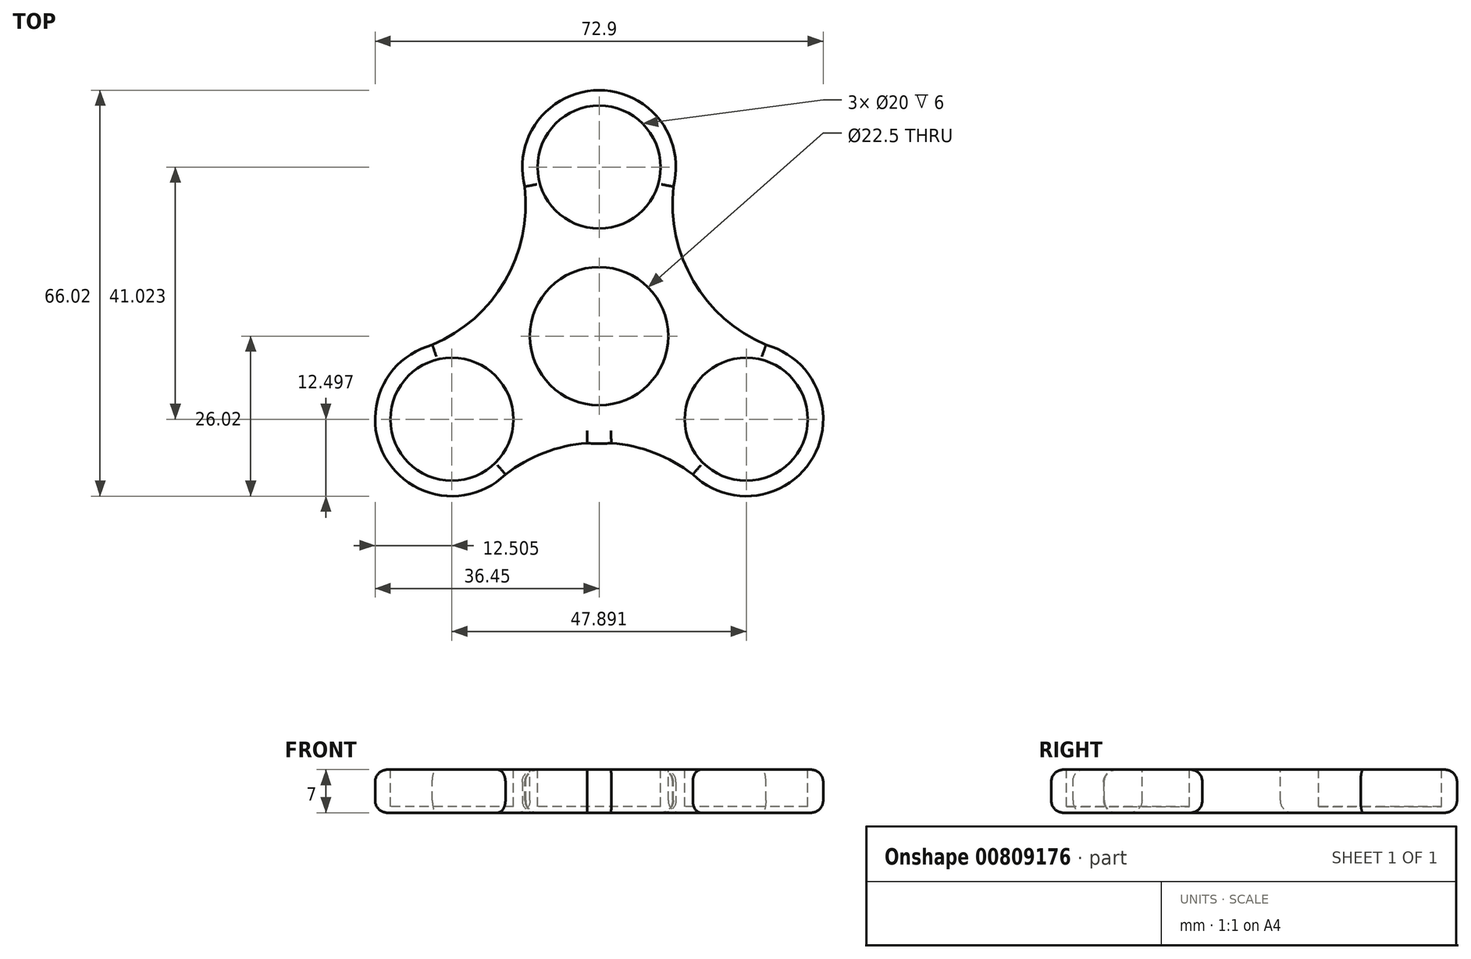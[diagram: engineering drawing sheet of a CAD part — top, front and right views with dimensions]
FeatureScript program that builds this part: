
annotation { "Feature Type Name" : "Feature", "Feature Type Description" : "" }
export const myFeature = defineFeature(function(context is Context, id is Id, definition is map)
    precondition{}
    {
        {
            var Q0;
            Q0=qCreatedBy(makeId("Top.planeOp"),FACE);
            var sketch = newSketch(context, id + "F0", { "sketchPlane" : qUnion([Q0])});
            skCircle(sketch, "E0", {"center": v(0, 0) * mm, "radius": 17.5 * mm});
            skCircle(sketch, "E1", {"center": v(0, 27.5) * mm, "radius": 12.5 * mm});
            skCircle(sketch, "E2", {"center": v(-23.95, -13.52) * mm, "radius": 12.5 * mm});
            skCircle(sketch, "E3", {"center": v(23.95, -13.52) * mm, "radius": 12.5 * mm});
            skSolve(sketch);
        }
        {
            var Q0;
            Q0 = qSketchRegion(id + "F0", true);
            extrude(context, id + "F1", {"entities" : qUnion([Q0]), "depth" : 7 * mm, "offsetDistance" : 25 * mm});
        }
        {
            var Q0;
            Q0=makeQuery(id+"F1.opExtrude","CAP_FACE",FACE,{"disambiguationData":[OSD([sQuery(id+"F0.wireOp",EDGE,"E0"),sQuery(id+"F0.wireOp",EDGE,"E1"),sQuery(id+"F0.wireOp",EDGE,"E2"),sQuery(id+"F0.wireOp",EDGE,"E3")])],"isStart":false});
            var sketch = newSketch(context, id + "F2", { "sketchPlane" : qUnion([Q0])});
            skCircle(sketch, "E4", {"center": v(0, 0) * mm, "radius": 11.25 * mm});
            skSolve(sketch);
        }
        {
            var Q0;
            Q0 = qSketchRegion(id + "F2", true);
            extrude(context, id + "F3", {"entities" : qUnion([Q0]), "operationType" : NewBodyOperationType.REMOVE, "endBound" : BoundingType.THROUGH_ALL, "oppositeDirection" : true, "depth" : 25 * mm, "offsetDistance" : 25 * mm});
        }
        {
            var Q0;
            Q0=makeQuery(id+"F1.opExtrude","CAP_FACE",FACE,{"disambiguationData":[OSD([sQuery(id+"F0.wireOp",EDGE,"E0"),sQuery(id+"F0.wireOp",EDGE,"E1"),sQuery(id+"F0.wireOp",EDGE,"E2"),sQuery(id+"F0.wireOp",EDGE,"E3")])],"isStart":false});
            var sketch = newSketch(context, id + "F4", { "sketchPlane" : qUnion([Q0])});
            skCircle(sketch, "E5", {"center": v(0, 27.5) * mm, "radius": 10 * mm});
            skCircle(sketch, "E6", {"center": v(23.95, -13.52) * mm, "radius": 10 * mm});
            skCircle(sketch, "E7", {"center": v(-23.95, -13.52) * mm, "radius": 10 * mm});
            skSolve(sketch);
        }
        {
            var Q0;
            Q0 = qSketchRegion(id + "F4", true);
            extrude(context, id + "F5", {"entities" : qUnion([Q0]), "operationType" : NewBodyOperationType.REMOVE, "oppositeDirection" : true, "depth" : 6 * mm, "offsetDistance" : 25 * mm});
        }
        {
            var Q0;
            Q0=makeQuery(id+"F1.opExtrude","CAP_FACE",FACE,{"disambiguationData":[OSD([sQuery(id+"F0.wireOp",EDGE,"E0"),sQuery(id+"F0.wireOp",EDGE,"E1"),sQuery(id+"F0.wireOp",EDGE,"E2"),sQuery(id+"F0.wireOp",EDGE,"E3")])],"isStart":false});
            var sketch = newSketch(context, id + "F6", { "sketchPlane" : qUnion([Q0])});
            skArc(sketch, "E8", {"start": v(15.24, -22.5) * mm, "mid": v(0, -17.31) * mm, "end": v(-15.24, -22.5) * mm});
            skArc(sketch, "E9", {"start": v(-27.13, -1.43) * mm, "mid": v(-15.35, 8.96) * mm, "end": v(-12.1, 24.33) * mm});
            skArc(sketch, "E10", {"start": v(12.1, 24.33) * mm, "mid": v(15.35, 8.96) * mm, "end": v(27.13, -1.43) * mm});
            skSolve(sketch);
        }
        {
            var Q0;
            {var subQ0=sQuery(id+"F6.wireOp",EDGE,"E9");Q0=makeQuery(id+"F6.imprint","IMPRINT",FACE,{"disambiguationData":[TD([[makeQuery(id+"F6.imprint","IMPRINT",EDGE,{"derivedFrom":subQ0}),-1.0]])]});}
            var Q1;
            {var subQ0=sQuery(id+"F6.wireOp",EDGE,"E8");var subQ1=sQuery(id+"F0.wireOp",EDGE,"E2");var subQ2=makeQuery(id+"F1.opExtrude","CAP_EDGE",EDGE,{"disambiguationData":[OSD([subQ1])],"isStart":false});var subQ3=makeQuery(id+"F6.imprint","INTERSECT",VERTEX,{"derivedFrom":[subQ2,subQ0]});Q1=makeQuery(id+"F6.imprint","IMPRINT",FACE,{"disambiguationData":[TD([[makeQuery(id+"F6.imprint","IMPRINT",EDGE,{"disambiguationData":[TD([[subQ3,1.0]])],"derivedFrom":subQ0}),-1.0]])]});}
            var Q2;
            {var subQ0=sQuery(id+"F6.wireOp",EDGE,"E8");var subQ1=sQuery(id+"F0.wireOp",EDGE,"E3");var subQ2=makeQuery(id+"F1.opExtrude","CAP_EDGE",EDGE,{"disambiguationData":[OSD([subQ1])],"isStart":false});var subQ3=makeQuery(id+"F6.imprint","INTERSECT",VERTEX,{"derivedFrom":[subQ2,subQ0]});Q2=makeQuery(id+"F6.imprint","IMPRINT",FACE,{"disambiguationData":[TD([[makeQuery(id+"F6.imprint","IMPRINT",EDGE,{"disambiguationData":[TD([[subQ3,-1.0]])],"derivedFrom":subQ0}),-1.0]])]});}
            var Q3;
            {var subQ0=sQuery(id+"F6.wireOp",EDGE,"E10");Q3=makeQuery(id+"F6.imprint","IMPRINT",FACE,{"disambiguationData":[TD([[makeQuery(id+"F6.imprint","IMPRINT",EDGE,{"derivedFrom":subQ0}),-1.0]])]});}
            extrude(context, id + "F7", {"entities" : qUnion([Q0, Q1, Q2, Q3]), "operationType" : NewBodyOperationType.ADD, "oppositeDirection" : true, "depth" : 7 * mm, "offsetDistance" : 25 * mm});
        }
        {
            var Q0;
            Q0=makeQuery(id+"F7.opExtrude","CAP_EDGE",EDGE,{"disambiguationData":[OSD([sQuery(id+"F6.wireOp",EDGE,"E10")])],"isStart":true});
            var Q1;
            Q1=makeQuery(id+"F1.opExtrude","CAP_EDGE",EDGE,{"disambiguationData":[OSD([sQuery(id+"F0.wireOp",EDGE,"E1")])],"isStart":false});
            var Q2;
            Q2=makeQuery(id+"F7.opExtrude","CAP_EDGE",EDGE,{"disambiguationData":[OSD([sQuery(id+"F6.wireOp",EDGE,"E9")])],"isStart":true});
            var Q3;
            {var subQ0=sQuery(id+"F6.wireOp",EDGE,"E8");var subQ1=sQuery(id+"F0.wireOp",EDGE,"E3");Q3=makeQuery(id+"F7.opExtrude","CAP_EDGE",EDGE,{"disambiguationData":[OSD([subQ0]),TDD([makeQuery(id+"F6.imprint","IMPRINT",EDGE,{"disambiguationData":[TD([[makeQuery(id+"F6.imprint","INTERSECT",VERTEX,{"derivedFrom":[makeQuery(id+"F1.opExtrude","CAP_EDGE",EDGE,{"disambiguationData":[OSD([subQ1])],"isStart":false}),subQ0]}),-1.0]])],"derivedFrom":subQ0})])],"isStart":true});}
            var Q4;
            Q4=makeQuery(id+"F1.opExtrude","CAP_EDGE",EDGE,{"disambiguationData":[OSD([sQuery(id+"F0.wireOp",EDGE,"E3")])],"isStart":false});
            var Q5;
            {var subQ0=sQuery(id+"F6.wireOp",EDGE,"E8");var subQ1=sQuery(id+"F0.wireOp",EDGE,"E2");Q5=makeQuery(id+"F7.opExtrude","CAP_EDGE",EDGE,{"disambiguationData":[OSD([subQ0]),TDD([makeQuery(id+"F6.imprint","IMPRINT",EDGE,{"disambiguationData":[TD([[makeQuery(id+"F6.imprint","INTERSECT",VERTEX,{"derivedFrom":[makeQuery(id+"F1.opExtrude","CAP_EDGE",EDGE,{"disambiguationData":[OSD([subQ1])],"isStart":false}),subQ0]}),1.0]])],"derivedFrom":subQ0})])],"isStart":true});}
            var Q6;
            {var subQ0=sQuery(id+"F0.wireOp",EDGE,"E0");Q6=makeQuery(id+"F1.opExtrude","CAP_EDGE",EDGE,{"disambiguationData":[OSD([subQ0]),TDD([makeQuery(id+"F0.imprint","IMPRINT",EDGE,{"disambiguationData":[TD([[makeQuery(id+"F0.imprint","INTERSECT",VERTEX,{"disambiguationData":[OD(1.0)],"derivedFrom":[subQ0,sQuery(id+"F0.wireOp",EDGE,"E2")]}),-1.0]])],"derivedFrom":subQ0})])],"isStart":false});}
            var Q7;
            Q7=makeQuery(id+"F1.opExtrude","CAP_EDGE",EDGE,{"disambiguationData":[OSD([sQuery(id+"F0.wireOp",EDGE,"E2")])],"isStart":false});
            var Q8;
            Q8=makeQuery(id+"F1.opExtrude","CAP_EDGE",EDGE,{"disambiguationData":[OSD([sQuery(id+"F0.wireOp",EDGE,"E3")])],"isStart":true});
            var Q9;
            Q9=makeQuery(id+"F1.opExtrude","CAP_EDGE",EDGE,{"disambiguationData":[OSD([sQuery(id+"F0.wireOp",EDGE,"E1")])],"isStart":true});
            var Q10;
            Q10=makeQuery(id+"F1.opExtrude","CAP_EDGE",EDGE,{"disambiguationData":[OSD([sQuery(id+"F0.wireOp",EDGE,"E2")])],"isStart":true});
            var Q11;
            {var subQ0=sQuery(id+"F6.wireOp",EDGE,"E8");var subQ1=sQuery(id+"F0.wireOp",EDGE,"E3");Q11=makeQuery(id+"F7.opExtrude","CAP_EDGE",EDGE,{"disambiguationData":[OSD([subQ0]),TDD([makeQuery(id+"F6.imprint","IMPRINT",EDGE,{"disambiguationData":[TD([[makeQuery(id+"F6.imprint","INTERSECT",VERTEX,{"derivedFrom":[makeQuery(id+"F1.opExtrude","CAP_EDGE",EDGE,{"disambiguationData":[OSD([subQ1])],"isStart":false}),subQ0]}),-1.0]])],"derivedFrom":subQ0})])],"isStart":false});}
            var Q12;
            {var subQ0=sQuery(id+"F0.wireOp",EDGE,"E0");Q12=makeQuery(id+"F1.opExtrude","CAP_EDGE",EDGE,{"disambiguationData":[OSD([subQ0]),TDD([makeQuery(id+"F0.imprint","IMPRINT",EDGE,{"disambiguationData":[TD([[makeQuery(id+"F0.imprint","INTERSECT",VERTEX,{"disambiguationData":[OD(1.0)],"derivedFrom":[subQ0,sQuery(id+"F0.wireOp",EDGE,"E2")]}),-1.0]])],"derivedFrom":subQ0})])],"isStart":true});}
            var Q13;
            {var subQ0=sQuery(id+"F6.wireOp",EDGE,"E8");var subQ1=sQuery(id+"F0.wireOp",EDGE,"E2");Q13=makeQuery(id+"F7.opExtrude","CAP_EDGE",EDGE,{"disambiguationData":[OSD([subQ0]),TDD([makeQuery(id+"F6.imprint","IMPRINT",EDGE,{"disambiguationData":[TD([[makeQuery(id+"F6.imprint","INTERSECT",VERTEX,{"derivedFrom":[makeQuery(id+"F1.opExtrude","CAP_EDGE",EDGE,{"disambiguationData":[OSD([subQ1])],"isStart":false}),subQ0]}),1.0]])],"derivedFrom":subQ0})])],"isStart":false});}
            var Q14;
            Q14=makeQuery(id+"F7.opExtrude","CAP_EDGE",EDGE,{"disambiguationData":[OSD([sQuery(id+"F6.wireOp",EDGE,"E9")])],"isStart":false});
            var Q15;
            Q15=makeQuery(id+"F7.opExtrude","CAP_EDGE",EDGE,{"disambiguationData":[OSD([sQuery(id+"F6.wireOp",EDGE,"E10")])],"isStart":false});
            var Q16;
            Q16=makeQuery(id+"F3.boolean.opBoolean","COPY",EDGE,{"derivedFrom":makeQuery(id+"F3.opExtrude","CAP_EDGE",EDGE,{"disambiguationData":[OSD([sQuery(id+"F2.wireOp",EDGE,"E4")])],"isStart":true})});
            var Q17;
            Q17=makeQuery(id+"F3.boolean.opBoolean","INTERSECT",EDGE,{"derivedFrom":[makeQuery(id+"F1.opExtrude","CAP_FACE",FACE,{"disambiguationData":[OSD([sQuery(id+"F0.wireOp",EDGE,"E0"),sQuery(id+"F0.wireOp",EDGE,"E1"),sQuery(id+"F0.wireOp",EDGE,"E2"),sQuery(id+"F0.wireOp",EDGE,"E3")])],"isStart":true}),makeQuery(id+"F3.opExtrude","SWEPT_FACE",FACE,{"disambiguationData":[OSD([sQuery(id+"F2.wireOp",EDGE,"E4")])]})]});
            fillet(context, id + "F8", {"entities" : qUnion([Q0, Q1, Q2, Q3, Q4, Q5, Q6, Q7, Q8, Q9, Q10, Q11, Q12, Q13, Q14, Q15, Q16, Q17]), "radius" : 2 * mm, "tangentPropagation" : true, "allowEdgeOverflow" : false});
        }
    });
